# Revit family: Grohe_EurosmartCosmopolitanT_ShowerMixer_36321000
name_source: partatom
category: Plumbing Fixtures
revit_build: Autodesk Revit 2018 (Build: 20190510_1515(x64)
units: mm (PartAtom-declared; Revit-internal decimal feet)

## family parameters
Cut with Voids When Loaded = No
Host = Face
OmniClass Number = 23.65.05.11.11
OmniClass Title = Water Supply Systems
Part Type = Normal
Room Calculation Point = No
Round Connector Dimension = Use Diameter
Shared = No

## types (1)
- 36321000
    Assembly Code = C1030200
    AssetType = Fixed
    BIMObjectName = Grohe_EurosmartCosmopolitanT_ShowerMixer_36321000
    CO2NeutralProduction = GROHE is one of the first leading manufacturer within the sanitary industry having a CO2-neutral production.
    ClassificationName = Uniclass2015
    ClassificationValue = Pr_40_20_87_07
    Color = Chrome
    Cost = 0 $
    Default Elevation = 0 mm  [stored 0 ft]
    Description = A functional fusion of minimalist design and user-friendly technology! With its sleek lines the self-closing GROHE Eurosmart Cosmopolitan T shower mixer mixing device complements any modern bathroom. Built to last with GROHE’s innovative technology, it has a built-in temperature limiter and three adjustable flow times of 7, 15 and 30 seconds* which reduce water wastage and any risk of flooding. It is a delight to use and comes with a mixing device that adjusts the water temperature.
    DocumentationCertificates = https://www.bimstore.co
    DocumentationInstallationGuide = https://www.bimstore.co
    DocumentationLiterature = https://www.bimstore.co
    DocumentationMaintenance = https://www.bimstore.co
    DocumentationTechnical = https://www.bimstore.co
    DurationUnit = Years
    EF000003 = Wall built-in
    EF000139 = Chromium-plated
    EF002147 = Hand
    EF002286 = Hose (gland nut)
    EF002671 = Chrome
    EF006974 = Manually operated
    EF020781 = Top section, non-ceramic
    EF020785 = 3/8 inch
    EF020791 = Brass
    EF024897 = Glossy
    EF025099 = 7-30
    ExpectedLife = 0
    FullRecyclabilityOfPlastic = All plastic components are fully recycable
    GROHESocialCommittment = green.grohe.com/social_engagement
    GROHESustainability = green.grohe.com
    IfcExportAs = IfcPipeFitting
    IfcExportType = IfcPipeFittingType
    Keynote = N13
    Manufacturer = Grohe
    ManufacturerName = Grohe
    Material = Chrome
    Model = Eurosmart Cosmopolitan T Shower Mixer
    ModelNumber = 36321000
    ModelReference = Nova Cosmopolitan S Flush Plate
    NBSDescription = Water supply fittings
    NBSObjectName = Grohe - Water supply fittings
    NBSReference = 45-35-70/315
    NominalDepth = 10.5 mm
    NominalHeight = 195 mm  [stored 0.639764 ft]
    NominalLength = 120 mm  [stored 0.393701 ft]
    ProductNumber = 36321000
    ProductionYear = 2021
    Size = 195mm(H)x120mm(W)x10mm(D)
    SustainabilityAward = green.grohe.com/awards
    SustainabilityReport = green.grohe.com/reporting
    Type Comments = 36321000
    TypeName = Eurosmart Cosmopolitan T Shower Mixer
    URL = https://www.grohe.co.uk
    WarrantyDurationLabor = 0
    WarrantyDurationParts = 0
    WarrantyDurationUnit = Years
    WarrantyGuarantorLabor = https://www.grohe.co.uk
    WarrantyGuarantorParts = https://www.grohe.co.uk
    _BSBibleVersion = 16
    _BimSpecGuid = 0
    _CurrentRevision = 1
    _DistributedBy = https://www.bimstore.co
    _ObjectUserGuide = https://www.bimstore.co

note: [stored X ft] marks values corroborated as IEEE doubles in the binary element streams (Revit-internal decimal feet)

## geometry (parser evidence)
native form markers: Sweep x2
no freeform markers — native parametric forms only
